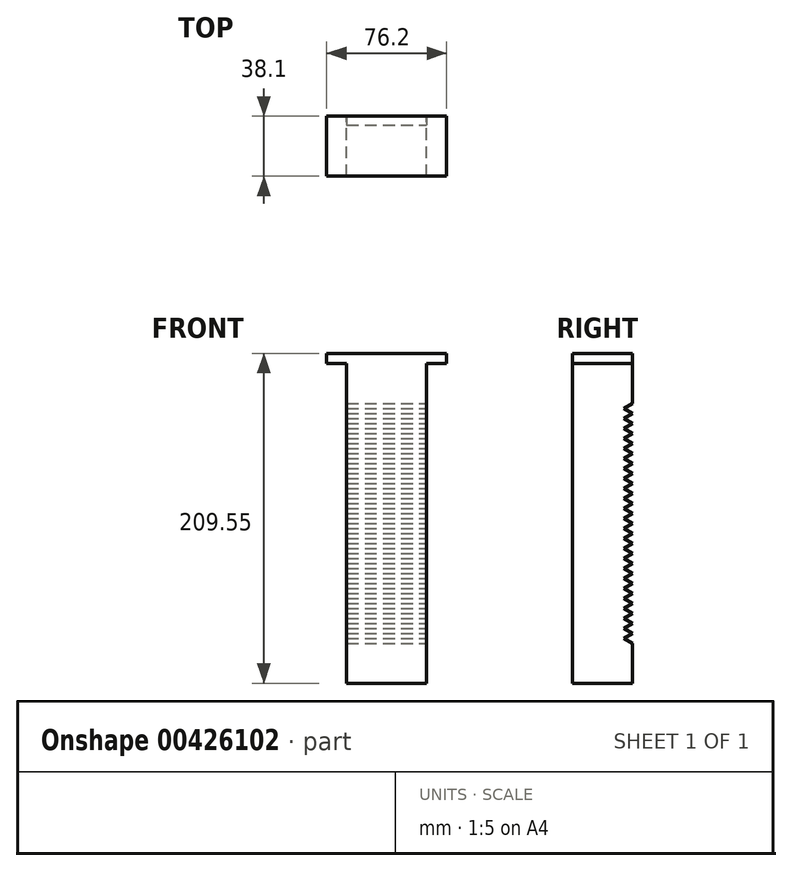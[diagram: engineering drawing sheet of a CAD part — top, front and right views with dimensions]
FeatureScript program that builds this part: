
annotation { "Feature Type Name" : "Feature", "Feature Type Description" : "" }
export const myFeature = defineFeature(function(context is Context, id is Id, definition is map)
    precondition{}
    {
        {
            var Q0;
            Q0=qCreatedBy(makeId("Front.planeOp"),FACE);
            var sketch = newSketch(context, id + "F0", { "sketchPlane" : qUnion([Q0])});
            skLineSegment(sketch, "E0", {"start": v(-25.4, 203.2) * mm, "end": v(25.4, 203.2) * mm});
            skLineSegment(sketch, "E1", {"start": v(25.4, 203.2) * mm, "end": v(25.4, 0) * mm});
            skLineSegment(sketch, "E2", {"start": v(25.4, 0) * mm, "end": v(-25.4, 0) * mm});
            skLineSegment(sketch, "E3", {"start": v(-25.4, 0) * mm, "end": v(-25.4, 203.2) * mm});
            skPoint(sketch, "E4", {"position": v(0, 203.2) * mm});
            skLineSegment(sketch, "E5", {"start": v(-38.1, 209.55) * mm, "end": v(-38.1, 203.2) * mm});
            skLineSegment(sketch, "E6", {"start": v(-38.1, 203.2) * mm, "end": v(38.1, 203.2) * mm});
            skLineSegment(sketch, "E7", {"start": v(38.1, 203.2) * mm, "end": v(38.1, 209.55) * mm});
            skLineSegment(sketch, "E8", {"start": v(38.1, 209.55) * mm, "end": v(-38.1, 209.55) * mm});
            skSolve(sketch);
        }
        {
            var Q0;
            {var subQ4=sQuery(id+"F0.wireOp",EDGE,"E5");Q0=makeQuery(id+"F0.imprint","IMPRINT",FACE,{"disambiguationData":[TD([[makeQuery(id+"F0.imprint","IMPRINT",EDGE,{"derivedFrom":subQ4}),1.0]])]});}
            var Q1;
            {var subQ0=sQuery(id+"F0.wireOp",EDGE,"E1");Q1=makeQuery(id+"F0.imprint","IMPRINT",FACE,{"disambiguationData":[TD([[makeQuery(id+"F0.imprint","IMPRINT",EDGE,{"derivedFrom":subQ0}),-1.0]])]});}
            extrude(context, id + "F1", {"entities" : qUnion([Q0, Q1]), "endBound" : BoundingType.SYMMETRIC, "depth" : 38.1 * mm});
        }
        {
            var Q0;
            Q0=makeQuery(id+"F1.opExtrude","SWEPT_FACE",FACE,{"disambiguationData":[OSD([sQuery(id+"F0.wireOp",EDGE,"E1")])]});
            var sketch = newSketch(context, id + "F2", { "sketchPlane" : qUnion([Q0])});
            skLineSegment(sketch, "E9", {"start": v(19.05, 203.2) * mm, "end": v(19.05, 177.8) * mm, "construction": true});
            skLineSegment(sketch, "E10", {"start": v(19.05, 0) * mm, "end": v(19.05, 25.4) * mm, "construction": true});
            skLineSegment(sketch, "E11", {"start": v(19.05, 25.4) * mm, "end": v(-19.05, 25.4) * mm, "construction": true});
            skLineSegment(sketch, "E12", {"start": v(19.05, 177.8) * mm, "end": v(-19.05, 177.8) * mm, "construction": true});
            skLineSegment(sketch, "E13", {"start": v(19.05, 177.8) * mm, "end": v(13.55, 174.63) * mm});
            skLineSegment(sketch, "E14", {"start": v(13.55, 174.63) * mm, "end": v(19.05, 171.45) * mm});
            skLineSegment(sketch, "E15", {"start": v(19.05, 171.45) * mm, "end": v(19.05, 177.8) * mm});
            skLineSegment(sketch, "E16.0.1.0", {"start": v(13.55, 168.28) * mm, "end": v(19.05, 165.1) * mm});
            skLineSegment(sketch, "E16.0.1.1", {"start": v(19.05, 171.45) * mm, "end": v(13.55, 168.28) * mm});
            skLineSegment(sketch, "E16.0.1.2", {"start": v(19.05, 165.1) * mm, "end": v(19.05, 171.45) * mm});
            skLineSegment(sketch, "E16.0.2.0", {"start": v(13.55, 161.93) * mm, "end": v(19.05, 158.75) * mm});
            skLineSegment(sketch, "E16.0.2.1", {"start": v(19.05, 165.1) * mm, "end": v(13.55, 161.93) * mm});
            skLineSegment(sketch, "E16.0.2.2", {"start": v(19.05, 158.75) * mm, "end": v(19.05, 165.1) * mm});
            skLineSegment(sketch, "E16.0.3.0", {"start": v(13.55, 155.58) * mm, "end": v(19.05, 152.4) * mm});
            skLineSegment(sketch, "E16.0.3.1", {"start": v(19.05, 158.75) * mm, "end": v(13.55, 155.58) * mm});
            skLineSegment(sketch, "E16.0.3.2", {"start": v(19.05, 152.4) * mm, "end": v(19.05, 158.75) * mm});
            skLineSegment(sketch, "E16.0.4.0", {"start": v(13.55, 149.23) * mm, "end": v(19.05, 146.05) * mm});
            skLineSegment(sketch, "E16.0.4.1", {"start": v(19.05, 152.4) * mm, "end": v(13.55, 149.23) * mm});
            skLineSegment(sketch, "E16.0.4.2", {"start": v(19.05, 146.05) * mm, "end": v(19.05, 152.4) * mm});
            skLineSegment(sketch, "E16.0.5.0", {"start": v(13.55, 142.88) * mm, "end": v(19.05, 139.7) * mm});
            skLineSegment(sketch, "E16.0.5.1", {"start": v(19.05, 146.05) * mm, "end": v(13.55, 142.88) * mm});
            skLineSegment(sketch, "E16.0.5.2", {"start": v(19.05, 139.7) * mm, "end": v(19.05, 146.05) * mm});
            skLineSegment(sketch, "E16.0.6.0", {"start": v(13.55, 136.53) * mm, "end": v(19.05, 133.35) * mm});
            skLineSegment(sketch, "E16.0.6.1", {"start": v(19.05, 139.7) * mm, "end": v(13.55, 136.53) * mm});
            skLineSegment(sketch, "E16.0.6.2", {"start": v(19.05, 133.35) * mm, "end": v(19.05, 139.7) * mm});
            skLineSegment(sketch, "E16.0.7.0", {"start": v(13.55, 130.18) * mm, "end": v(19.05, 127) * mm});
            skLineSegment(sketch, "E16.0.7.1", {"start": v(19.05, 133.35) * mm, "end": v(13.55, 130.18) * mm});
            skLineSegment(sketch, "E16.0.7.2", {"start": v(19.05, 127) * mm, "end": v(19.05, 133.35) * mm});
            skLineSegment(sketch, "E16.0.8.0", {"start": v(13.55, 123.83) * mm, "end": v(19.05, 120.65) * mm});
            skLineSegment(sketch, "E16.0.8.1", {"start": v(19.05, 127) * mm, "end": v(13.55, 123.83) * mm});
            skLineSegment(sketch, "E16.0.8.2", {"start": v(19.05, 120.65) * mm, "end": v(19.05, 127) * mm});
            skLineSegment(sketch, "E16.0.9.0", {"start": v(13.55, 117.48) * mm, "end": v(19.05, 114.3) * mm});
            skLineSegment(sketch, "E16.0.9.1", {"start": v(19.05, 120.65) * mm, "end": v(13.55, 117.48) * mm});
            skLineSegment(sketch, "E16.0.9.2", {"start": v(19.05, 114.3) * mm, "end": v(19.05, 120.65) * mm});
            skLineSegment(sketch, "E16.0.10.0", {"start": v(13.55, 111.13) * mm, "end": v(19.05, 107.95) * mm});
            skLineSegment(sketch, "E16.0.10.1", {"start": v(19.05, 114.3) * mm, "end": v(13.55, 111.13) * mm});
            skLineSegment(sketch, "E16.0.10.2", {"start": v(19.05, 107.95) * mm, "end": v(19.05, 114.3) * mm});
            skLineSegment(sketch, "E16.0.11.0", {"start": v(13.55, 104.78) * mm, "end": v(19.05, 101.6) * mm});
            skLineSegment(sketch, "E16.0.11.1", {"start": v(19.05, 107.95) * mm, "end": v(13.55, 104.78) * mm});
            skLineSegment(sketch, "E16.0.11.2", {"start": v(19.05, 101.6) * mm, "end": v(19.05, 107.95) * mm});
            skLineSegment(sketch, "E16.0.12.0", {"start": v(13.55, 98.43) * mm, "end": v(19.05, 95.25) * mm});
            skLineSegment(sketch, "E16.0.12.1", {"start": v(19.05, 101.6) * mm, "end": v(13.55, 98.43) * mm});
            skLineSegment(sketch, "E16.0.12.2", {"start": v(19.05, 95.25) * mm, "end": v(19.05, 101.6) * mm});
            skLineSegment(sketch, "E16.0.13.0", {"start": v(13.55, 92.08) * mm, "end": v(19.05, 88.9) * mm});
            skLineSegment(sketch, "E16.0.13.1", {"start": v(19.05, 95.25) * mm, "end": v(13.55, 92.08) * mm});
            skLineSegment(sketch, "E16.0.13.2", {"start": v(19.05, 88.9) * mm, "end": v(19.05, 95.25) * mm});
            skLineSegment(sketch, "E16.0.14.0", {"start": v(13.55, 85.73) * mm, "end": v(19.05, 82.55) * mm});
            skLineSegment(sketch, "E16.0.14.1", {"start": v(19.05, 88.9) * mm, "end": v(13.55, 85.73) * mm});
            skLineSegment(sketch, "E16.0.14.2", {"start": v(19.05, 82.55) * mm, "end": v(19.05, 88.9) * mm});
            skLineSegment(sketch, "E16.0.15.0", {"start": v(13.55, 79.38) * mm, "end": v(19.05, 76.2) * mm});
            skLineSegment(sketch, "E16.0.15.1", {"start": v(19.05, 82.55) * mm, "end": v(13.55, 79.38) * mm});
            skLineSegment(sketch, "E16.0.15.2", {"start": v(19.05, 76.2) * mm, "end": v(19.05, 82.55) * mm});
            skLineSegment(sketch, "E16.0.16.0", {"start": v(13.55, 73.03) * mm, "end": v(19.05, 69.85) * mm});
            skLineSegment(sketch, "E16.0.16.1", {"start": v(19.05, 76.2) * mm, "end": v(13.55, 73.03) * mm});
            skLineSegment(sketch, "E16.0.16.2", {"start": v(19.05, 69.85) * mm, "end": v(19.05, 76.2) * mm});
            skLineSegment(sketch, "E16.0.17.0", {"start": v(13.55, 66.68) * mm, "end": v(19.05, 63.5) * mm});
            skLineSegment(sketch, "E16.0.17.1", {"start": v(19.05, 69.85) * mm, "end": v(13.55, 66.68) * mm});
            skLineSegment(sketch, "E16.0.17.2", {"start": v(19.05, 63.5) * mm, "end": v(19.05, 69.85) * mm});
            skLineSegment(sketch, "E16.0.18.0", {"start": v(13.55, 60.33) * mm, "end": v(19.05, 57.15) * mm});
            skLineSegment(sketch, "E16.0.18.1", {"start": v(19.05, 63.5) * mm, "end": v(13.55, 60.33) * mm});
            skLineSegment(sketch, "E16.0.18.2", {"start": v(19.05, 57.15) * mm, "end": v(19.05, 63.5) * mm});
            skLineSegment(sketch, "E16.0.19.0", {"start": v(13.55, 53.98) * mm, "end": v(19.05, 50.8) * mm});
            skLineSegment(sketch, "E16.0.19.1", {"start": v(19.05, 57.15) * mm, "end": v(13.55, 53.98) * mm});
            skLineSegment(sketch, "E16.0.19.2", {"start": v(19.05, 50.8) * mm, "end": v(19.05, 57.15) * mm});
            skLineSegment(sketch, "E16.0.20.0", {"start": v(13.55, 47.63) * mm, "end": v(19.05, 44.45) * mm});
            skLineSegment(sketch, "E16.0.20.1", {"start": v(19.05, 50.8) * mm, "end": v(13.55, 47.63) * mm});
            skLineSegment(sketch, "E16.0.20.2", {"start": v(19.05, 44.45) * mm, "end": v(19.05, 50.8) * mm});
            skLineSegment(sketch, "E16.0.21.0", {"start": v(13.55, 41.28) * mm, "end": v(19.05, 38.1) * mm});
            skLineSegment(sketch, "E16.0.21.1", {"start": v(19.05, 44.45) * mm, "end": v(13.55, 41.28) * mm});
            skLineSegment(sketch, "E16.0.21.2", {"start": v(19.05, 38.1) * mm, "end": v(19.05, 44.45) * mm});
            skLineSegment(sketch, "E16.0.22.0", {"start": v(13.55, 34.93) * mm, "end": v(19.05, 31.75) * mm});
            skLineSegment(sketch, "E16.0.22.1", {"start": v(19.05, 38.1) * mm, "end": v(13.55, 34.93) * mm});
            skLineSegment(sketch, "E16.0.22.2", {"start": v(19.05, 31.75) * mm, "end": v(19.05, 38.1) * mm});
            skLineSegment(sketch, "E16.0.23.0", {"start": v(13.55, 28.58) * mm, "end": v(19.05, 25.4) * mm});
            skLineSegment(sketch, "E16.0.23.1", {"start": v(19.05, 31.75) * mm, "end": v(13.55, 28.58) * mm});
            skLineSegment(sketch, "E16.0.23.2", {"start": v(19.05, 25.4) * mm, "end": v(19.05, 31.75) * mm});
            skLineSegment(sketch, "E16.direction1", {"start": v(13.55, 174.63) * mm, "end": v(38.95, 174.63) * mm, "construction": true});
            skLineSegment(sketch, "E16.direction2", {"start": v(13.55, 174.63) * mm, "end": v(13.55, 168.28) * mm, "construction": true});
            skSolve(sketch);
        }
        {
            var Q0;
            Q0=makeQuery(id+"F2.imprint","IMPRINT",FACE,{"disambiguationData":[TD([[makeQuery(id+"F2.imprint","IMPRINT",EDGE,{"derivedFrom":sQuery(id+"F2.wireOp",EDGE,"E16.0.17.0")}),1.0]])]});
            var Q1;
            Q1=makeQuery(id+"F2.imprint","IMPRINT",FACE,{"disambiguationData":[TD([[makeQuery(id+"F2.imprint","IMPRINT",EDGE,{"derivedFrom":sQuery(id+"F2.wireOp",EDGE,"E16.0.23.0")}),1.0]])]});
            var Q2;
            Q2=makeQuery(id+"F2.imprint","IMPRINT",FACE,{"disambiguationData":[TD([[makeQuery(id+"F2.imprint","IMPRINT",EDGE,{"derivedFrom":sQuery(id+"F2.wireOp",EDGE,"E16.0.18.0")}),1.0]])]});
            var Q3;
            Q3=makeQuery(id+"F2.imprint","IMPRINT",FACE,{"disambiguationData":[TD([[makeQuery(id+"F2.imprint","IMPRINT",EDGE,{"derivedFrom":sQuery(id+"F2.wireOp",EDGE,"E16.0.15.0")}),1.0]])]});
            var Q4;
            Q4=makeQuery(id+"F2.imprint","IMPRINT",FACE,{"disambiguationData":[TD([[makeQuery(id+"F2.imprint","IMPRINT",EDGE,{"derivedFrom":sQuery(id+"F2.wireOp",EDGE,"E16.0.13.0")}),1.0]])]});
            var Q5;
            Q5=makeQuery(id+"F2.imprint","IMPRINT",FACE,{"disambiguationData":[TD([[makeQuery(id+"F2.imprint","IMPRINT",EDGE,{"derivedFrom":sQuery(id+"F2.wireOp",EDGE,"E16.0.14.0")}),1.0]])]});
            var Q6;
            Q6=makeQuery(id+"F2.imprint","IMPRINT",FACE,{"disambiguationData":[TD([[makeQuery(id+"F2.imprint","IMPRINT",EDGE,{"derivedFrom":sQuery(id+"F2.wireOp",EDGE,"E13")}),1.0]])]});
            var Q7;
            Q7=makeQuery(id+"F2.imprint","IMPRINT",FACE,{"disambiguationData":[TD([[makeQuery(id+"F2.imprint","IMPRINT",EDGE,{"derivedFrom":sQuery(id+"F2.wireOp",EDGE,"E16.0.1.0")}),1.0]])]});
            var Q8;
            Q8=makeQuery(id+"F2.imprint","IMPRINT",FACE,{"disambiguationData":[TD([[makeQuery(id+"F2.imprint","IMPRINT",EDGE,{"derivedFrom":sQuery(id+"F2.wireOp",EDGE,"E16.0.2.0")}),1.0]])]});
            var Q9;
            Q9=makeQuery(id+"F2.imprint","IMPRINT",FACE,{"disambiguationData":[TD([[makeQuery(id+"F2.imprint","IMPRINT",EDGE,{"derivedFrom":sQuery(id+"F2.wireOp",EDGE,"E16.0.3.0")}),1.0]])]});
            var Q10;
            Q10=makeQuery(id+"F2.imprint","IMPRINT",FACE,{"disambiguationData":[TD([[makeQuery(id+"F2.imprint","IMPRINT",EDGE,{"derivedFrom":sQuery(id+"F2.wireOp",EDGE,"E16.0.4.0")}),1.0]])]});
            var Q11;
            Q11=makeQuery(id+"F2.imprint","IMPRINT",FACE,{"disambiguationData":[TD([[makeQuery(id+"F2.imprint","IMPRINT",EDGE,{"derivedFrom":sQuery(id+"F2.wireOp",EDGE,"E16.0.5.0")}),1.0]])]});
            var Q12;
            Q12=makeQuery(id+"F2.imprint","IMPRINT",FACE,{"disambiguationData":[TD([[makeQuery(id+"F2.imprint","IMPRINT",EDGE,{"derivedFrom":sQuery(id+"F2.wireOp",EDGE,"E16.0.6.0")}),1.0]])]});
            var Q13;
            Q13=makeQuery(id+"F2.imprint","IMPRINT",FACE,{"disambiguationData":[TD([[makeQuery(id+"F2.imprint","IMPRINT",EDGE,{"derivedFrom":sQuery(id+"F2.wireOp",EDGE,"E16.0.7.0")}),1.0]])]});
            var Q14;
            Q14=makeQuery(id+"F2.imprint","IMPRINT",FACE,{"disambiguationData":[TD([[makeQuery(id+"F2.imprint","IMPRINT",EDGE,{"derivedFrom":sQuery(id+"F2.wireOp",EDGE,"E16.0.9.0")}),1.0]])]});
            var Q15;
            Q15=makeQuery(id+"F2.imprint","IMPRINT",FACE,{"disambiguationData":[TD([[makeQuery(id+"F2.imprint","IMPRINT",EDGE,{"derivedFrom":sQuery(id+"F2.wireOp",EDGE,"E16.0.8.0")}),1.0]])]});
            var Q16;
            Q16=makeQuery(id+"F2.imprint","IMPRINT",FACE,{"disambiguationData":[TD([[makeQuery(id+"F2.imprint","IMPRINT",EDGE,{"derivedFrom":sQuery(id+"F2.wireOp",EDGE,"E16.0.10.0")}),1.0]])]});
            var Q17;
            Q17=makeQuery(id+"F2.imprint","IMPRINT",FACE,{"disambiguationData":[TD([[makeQuery(id+"F2.imprint","IMPRINT",EDGE,{"derivedFrom":sQuery(id+"F2.wireOp",EDGE,"E16.0.11.0")}),1.0]])]});
            var Q18;
            Q18=makeQuery(id+"F2.imprint","IMPRINT",FACE,{"disambiguationData":[TD([[makeQuery(id+"F2.imprint","IMPRINT",EDGE,{"derivedFrom":sQuery(id+"F2.wireOp",EDGE,"E16.0.12.0")}),1.0]])]});
            var Q19;
            Q19=makeQuery(id+"F2.imprint","IMPRINT",FACE,{"disambiguationData":[TD([[makeQuery(id+"F2.imprint","IMPRINT",EDGE,{"derivedFrom":sQuery(id+"F2.wireOp",EDGE,"E16.0.22.0")}),1.0]])]});
            var Q20;
            Q20=makeQuery(id+"F2.imprint","IMPRINT",FACE,{"disambiguationData":[TD([[makeQuery(id+"F2.imprint","IMPRINT",EDGE,{"derivedFrom":sQuery(id+"F2.wireOp",EDGE,"E16.0.20.0")}),1.0]])]});
            var Q21;
            Q21=makeQuery(id+"F2.imprint","IMPRINT",FACE,{"disambiguationData":[TD([[makeQuery(id+"F2.imprint","IMPRINT",EDGE,{"derivedFrom":sQuery(id+"F2.wireOp",EDGE,"E16.0.16.0")}),1.0]])]});
            var Q22;
            Q22=makeQuery(id+"F2.imprint","IMPRINT",FACE,{"disambiguationData":[TD([[makeQuery(id+"F2.imprint","IMPRINT",EDGE,{"derivedFrom":sQuery(id+"F2.wireOp",EDGE,"E16.0.19.0")}),1.0]])]});
            var Q23;
            Q23=makeQuery(id+"F2.imprint","IMPRINT",FACE,{"disambiguationData":[TD([[makeQuery(id+"F2.imprint","IMPRINT",EDGE,{"derivedFrom":sQuery(id+"F2.wireOp",EDGE,"E16.0.21.0")}),1.0]])]});
            var Q24;
            Q24=sQuery(id+"F2.wireOp",EDGE,"E16.0.11.2");
            var Q25;
            Q25=sQuery(id+"F2.wireOp",EDGE,"E16.0.9.2");
            var Q26;
            Q26=sQuery(id+"F2.wireOp",EDGE,"E16.0.22.2");
            var Q27;
            Q27=sQuery(id+"F2.wireOp",EDGE,"E16.0.6.2");
            var Q28;
            Q28=sQuery(id+"F2.wireOp",EDGE,"E16.0.14.2");
            var Q29;
            Q29=sQuery(id+"F2.wireOp",EDGE,"E16.0.8.2");
            var Q30;
            Q30=sQuery(id+"F2.wireOp",EDGE,"E16.0.3.2");
            var Q31;
            Q31=sQuery(id+"F2.wireOp",EDGE,"E16.0.5.2");
            var Q32;
            Q32=sQuery(id+"F2.wireOp",EDGE,"E15");
            var Q33;
            Q33=sQuery(id+"F2.wireOp",EDGE,"E16.0.1.2");
            var Q34;
            Q34=sQuery(id+"F2.wireOp",EDGE,"E16.0.17.2");
            var Q35;
            Q35=sQuery(id+"F2.wireOp",EDGE,"E16.0.2.2");
            var Q36;
            Q36=sQuery(id+"F2.wireOp",EDGE,"E16.0.21.2");
            var Q37;
            Q37=sQuery(id+"F2.wireOp",EDGE,"E16.0.4.2");
            var Q38;
            Q38=sQuery(id+"F2.wireOp",EDGE,"E16.0.19.2");
            var Q39;
            Q39=sQuery(id+"F2.wireOp",EDGE,"E16.0.16.2");
            var Q40;
            Q40=sQuery(id+"F2.wireOp",EDGE,"E16.0.20.2");
            var Q41;
            Q41=sQuery(id+"F2.wireOp",EDGE,"E16.0.12.2");
            var Q42;
            Q42=sQuery(id+"F2.wireOp",EDGE,"E16.0.15.2");
            var Q43;
            Q43=sQuery(id+"F2.wireOp",EDGE,"E16.0.18.2");
            var Q44;
            Q44=sQuery(id+"F2.wireOp",EDGE,"E16.0.13.2");
            var Q45;
            Q45=sQuery(id+"F2.wireOp",EDGE,"E16.0.10.2");
            var Q46;
            Q46=sQuery(id+"F2.wireOp",EDGE,"E16.0.7.2");
            var Q47;
            Q47=sQuery(id+"F2.wireOp",EDGE,"E16.0.23.2");
            var Q48;
            Q48=sQuery(id+"F2.wireOp",EDGE,"E16.0.9.1");
            var Q49;
            Q49=sQuery(id+"F2.wireOp",EDGE,"E16.0.11.0");
            var Q50;
            Q50=sQuery(id+"F2.wireOp",EDGE,"E16.0.17.0");
            var Q51;
            Q51=sQuery(id+"F2.wireOp",EDGE,"E16.0.6.1");
            var Q52;
            Q52=sQuery(id+"F2.wireOp",EDGE,"E16.0.4.0");
            var Q53;
            Q53=sQuery(id+"F2.wireOp",EDGE,"E16.0.22.1");
            var Q54;
            Q54=sQuery(id+"F2.wireOp",EDGE,"E16.0.4.1");
            var Q55;
            Q55=sQuery(id+"F2.wireOp",EDGE,"E16.0.12.0");
            var Q56;
            Q56=sQuery(id+"F2.wireOp",EDGE,"E16.0.17.1");
            var Q57;
            Q57=sQuery(id+"F2.wireOp",EDGE,"E16.0.20.0");
            var Q58;
            Q58=sQuery(id+"F2.wireOp",EDGE,"E16.0.20.1");
            var Q59;
            Q59=sQuery(id+"F2.wireOp",EDGE,"E16.0.15.0");
            var Q60;
            Q60=sQuery(id+"F2.wireOp",EDGE,"E16.0.3.0");
            var Q61;
            Q61=sQuery(id+"F2.wireOp",EDGE,"E16.0.3.1");
            var Q62;
            Q62=sQuery(id+"F2.wireOp",EDGE,"E16.0.2.0");
            var Q63;
            Q63=sQuery(id+"F2.wireOp",EDGE,"E16.0.2.1");
            var Q64;
            Q64=sQuery(id+"F2.wireOp",EDGE,"E16.0.23.0");
            var Q65;
            Q65=sQuery(id+"F2.wireOp",EDGE,"E16.0.12.1");
            var Q66;
            Q66=sQuery(id+"F2.wireOp",EDGE,"E16.0.7.0");
            var Q67;
            Q67=sQuery(id+"F2.wireOp",EDGE,"E16.0.19.1");
            var Q68;
            Q68=sQuery(id+"F2.wireOp",EDGE,"E16.0.14.0");
            var Q69;
            Q69=sQuery(id+"F2.wireOp",EDGE,"E16.0.10.0");
            var Q70;
            Q70=sQuery(id+"F2.wireOp",EDGE,"E16.0.16.1");
            var Q71;
            Q71=sQuery(id+"F2.wireOp",EDGE,"E16.0.9.0");
            var Q72;
            Q72=sQuery(id+"F2.wireOp",EDGE,"E16.0.11.1");
            var Q73;
            Q73=sQuery(id+"F2.wireOp",EDGE,"E16.0.6.0");
            var Q74;
            Q74=sQuery(id+"F2.wireOp",EDGE,"E16.0.22.0");
            var Q75;
            Q75=sQuery(id+"F2.wireOp",EDGE,"E16.0.14.1");
            var Q76;
            Q76=sQuery(id+"F2.wireOp",EDGE,"E16.0.15.1");
            var Q77;
            Q77=sQuery(id+"F2.wireOp",EDGE,"E16.0.7.1");
            var Q78;
            Q78=sQuery(id+"F2.wireOp",EDGE,"E16.0.10.1");
            var Q79;
            Q79=sQuery(id+"F2.wireOp",EDGE,"E16.0.21.0");
            var Q80;
            Q80=sQuery(id+"F2.wireOp",EDGE,"E16.0.18.0");
            var Q81;
            Q81=sQuery(id+"F2.wireOp",EDGE,"E16.0.5.0");
            var Q82;
            Q82=sQuery(id+"F2.wireOp",EDGE,"E16.0.23.1");
            var Q83;
            Q83=sQuery(id+"F2.wireOp",EDGE,"E16.0.8.0");
            var Q84;
            Q84=sQuery(id+"F2.wireOp",EDGE,"E16.0.13.1");
            var Q85;
            Q85=sQuery(id+"F2.wireOp",EDGE,"E16.0.16.0");
            var Q86;
            Q86=sQuery(id+"F2.wireOp",EDGE,"E16.0.21.1");
            var Q87;
            Q87=sQuery(id+"F2.wireOp",EDGE,"E16.0.19.0");
            var Q88;
            Q88=sQuery(id+"F2.wireOp",EDGE,"E16.0.5.1");
            var Q89;
            Q89=sQuery(id+"F2.wireOp",EDGE,"E16.0.8.1");
            var Q90;
            Q90=sQuery(id+"F2.wireOp",EDGE,"E16.0.13.0");
            var Q91;
            Q91=sQuery(id+"F2.wireOp",EDGE,"E16.0.18.1");
            var Q92;
            Q92=sQuery(id+"F2.wireOp",EDGE,"E16.0.1.0");
            var Q93;
            Q93=sQuery(id+"F2.wireOp",EDGE,"E16.0.1.1");
            var Q94;
            Q94=sQuery(id+"F2.wireOp",EDGE,"E13");
            var Q95;
            Q95=sQuery(id+"F2.wireOp",EDGE,"E14");
            extrude(context, id + "F3", {"entities" : qUnion([Q0, Q1, Q2, Q3, Q4, Q5, Q6, Q7, Q8, Q9, Q10, Q11, Q12, Q13, Q14, Q15, Q16, Q17, Q18, Q19, Q20, Q21, Q22, Q23]), "operationType" : NewBodyOperationType.REMOVE, "surfaceEntities" : qUnion([Q24, Q25, Q26, Q27, Q28, Q29, Q30, Q31, Q32, Q33, Q34, Q35, Q36, Q37, Q38, Q39, Q40, Q41, Q42, Q43, Q44, Q45, Q46, Q47, Q48, Q49, Q50, Q51, Q52, Q53, Q54, Q55, Q56, Q57, Q58, Q59, Q60, Q61, Q62, Q63, Q64, Q65, Q66, Q67, Q68, Q69, Q70, Q71, Q72, Q73, Q74, Q75, Q76, Q77, Q78, Q79, Q80, Q81, Q82, Q83, Q84, Q85, Q86, Q87, Q88, Q89, Q90, Q91, Q92, Q93, Q94, Q95]), "oppositeDirection" : true, "depth" : 50.8 * mm});
        }
    });
